# Revit family: Legrand_Gestion_eclairage_Detecteur_Presence_Mur_KNX
name_source: partatom
category: Dispositifs d'éclairage
units: mm (PartAtom-declared; Revit-internal decimal feet)

## family parameters
Conserver l'orientation des annotations = Oui
Cote de connecteur circulaire = Utiliser le diamètre
Couper avec des vides une fois chargée = Non
Hôte = Face
Partagée = Non
Point de calcul de pièce = Non
Type d'élément = Normal

## types (2) — shared parameters
Adapté pour transmission sans fil = Non
Collecteur de terre = Non
Condition Générale d'Utilisation = https://export.legrand.com
Cosses d'artère secondaire = Non
Couleur = Blanc
Coupure forcée = Non
Durée d'enclenchement max. (mn) = 18
Durée d'enclenchement min. (s) = 5
Elévation par défaut = 2500 mm
Entrée secondaire = Non
Exécution - Modèle = détecteur de mouvement
Fabricant = Legrand
Fonction variateur intégré = Non
Gestion CVC = Non
Gestion alarme = Non
Hauteur de montage maximale (m) = 2.5
Liaison neutre = Non
Mode de montage = apparent
Numéro RAL = 9003
Réglage de lumière constante = Oui
Sensibilité lumineuse réglable = Oui
Sensibilité réglable = Oui
Télécommandable = Non
URL = http://www.legrandoc.com
zero-valued in all types: Angle de détection horizontal (MIN) (°), Capacité de coupure max. (W), Courant de démarrage max. (A), Fréquence (MAX) (Hz), Fréquence (MIN) (Hz), Sensibilité lumineuse (MAX) (lx), Sensibilité lumineuse (MIN) (lx), Température (MAX) (°C), Température (MIN) (°C), Tension nominale (V)

## per-type parameters (varying)
| type | Angle de détection horizontal (MAX) (°) | Description | Diamètre de détection sur le plancher (m) | Dual-tech KNX mural 180° | Modèle | PIR KNX mural 270°+180° | Portée max. frontale (m) | Portée max. latérale (m) |
| Dual-tech KNX mural 180° | 180 | Détecteur de présence BUS/KNX - fixation mur saillie - 8 m | 6 | Oui | 048920 | Non | 12 | 3 |
| PIR KNX mural 270°+180° | 270 | Détecteur de mouvement BUS/KNX - spécial parkings/extérieurs/caves - saillie | 10 | Non | 048921 | Oui | 15 | 5 |

## geometry (parser evidence)
native form markers: Blend x10
no freeform markers — native parametric forms only
